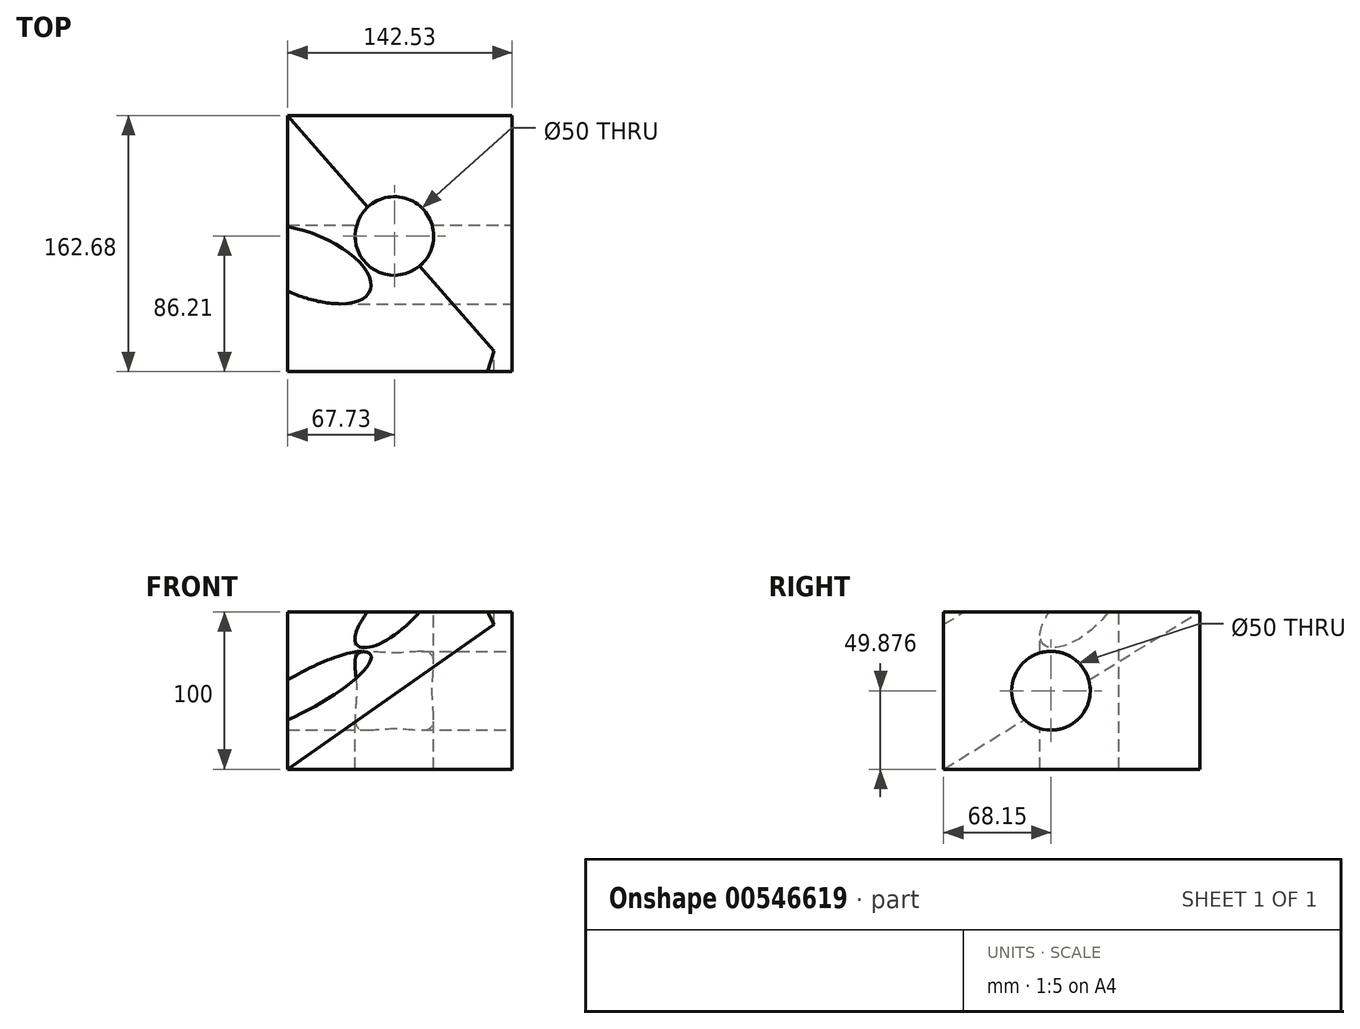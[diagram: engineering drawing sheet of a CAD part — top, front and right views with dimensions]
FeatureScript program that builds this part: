
annotation { "Feature Type Name" : "Feature", "Feature Type Description" : "" }
export const myFeature = defineFeature(function(context is Context, id is Id, definition is map)
    precondition{}
    {
        {
            var Q0;
            Q0=qCreatedBy(makeId("Top.planeOp"),FACE);
            var sketch = newSketch(context, id + "F0", { "sketchPlane" : qUnion([Q0])});
            skLineSegment(sketch, "E0.bottom", {"start": v(-67.73, -68.15) * mm, "end": v(74.8, -68.15) * mm});
            skLineSegment(sketch, "E0.top", {"start": v(-67.73, 94.53) * mm, "end": v(74.8, 94.53) * mm});
            skLineSegment(sketch, "E0.left", {"start": v(-67.73, -68.15) * mm, "end": v(-67.73, 94.53) * mm});
            skLineSegment(sketch, "E0.right", {"start": v(74.8, -68.15) * mm, "end": v(74.8, 94.53) * mm});
            skSolve(sketch);
        }
        {
            var Q0;
            Q0=makeQuery(id+"F0.imprint","IMPRINT",FACE,{"disambiguationData":[TD([[makeQuery(id+"F0.imprint","IMPRINT",EDGE,{"derivedFrom":sQuery(id+"F0.wireOp",EDGE,"E0.bottom")}),1.0]])]});
            extrude(context, id + "F1", {"entities" : qUnion([Q0]), "depth" : 100 * mm, "offsetDistance" : 25 * mm});
        }
        {
            var Q0;
            Q0=makeQuery(id+"F1.opExtrude","CAP_FACE",FACE,{"disambiguationData":[OSD([sQuery(id+"F0.wireOp",EDGE,"E0.bottom"),sQuery(id+"F0.wireOp",EDGE,"E0.top"),sQuery(id+"F0.wireOp",EDGE,"E0.left"),sQuery(id+"F0.wireOp",EDGE,"E0.right")])],"isStart":false});
            var sketch = newSketch(context, id + "F2", { "sketchPlane" : qUnion([Q0])});
            skPoint(sketch, "E1", {"position": v(0, 18.06) * mm});
            skSolve(sketch);
        }
        {
            var Q0;
            Q0=sQuery(id+"F2.wireOp",VERTEX,"E1");
            var Q1;
            Q1=makeQuery(id+"F1.opExtrude","SWEPT_BODY",BODY,{"disambiguationData":[OSD([sQuery(id+"F0.wireOp",EDGE,"E0.bottom"),sQuery(id+"F0.wireOp",EDGE,"E0.top"),sQuery(id+"F0.wireOp",EDGE,"E0.left"),sQuery(id+"F0.wireOp",EDGE,"E0.right")])]});
            hole(context, id + "F3", {"style" : HoleStyle.SIMPLE, "endStyle" : HoleEndStyle.THROUGH, "holeDiameter" : 50 * mm, "isTappedThrough" : true, "tappedDepth" : 12 * mm, "tapClearance" : 3, "locations" : qUnion([Q0]), "scope" : qUnion([Q1])});
        }
        {
            var Q0;
            Q0=makeQuery(id+"F1.opExtrude","SWEPT_FACE",FACE,{"disambiguationData":[OSD([sQuery(id+"F0.wireOp",EDGE,"E0.right")])]});
            var sketch = newSketch(context, id + "F4", { "sketchPlane" : qUnion([Q0])});
            skPoint(sketch, "E2", {"position": v(0, 49.88) * mm});
            skSolve(sketch);
        }
        {
            var Q0;
            Q0=sQuery(id+"F4.wireOp",VERTEX,"E2");
            var Q1;
            Q1=makeQuery(id+"F1.opExtrude","SWEPT_BODY",BODY,{"disambiguationData":[OSD([sQuery(id+"F0.wireOp",EDGE,"E0.bottom"),sQuery(id+"F0.wireOp",EDGE,"E0.top"),sQuery(id+"F0.wireOp",EDGE,"E0.left"),sQuery(id+"F0.wireOp",EDGE,"E0.right")])]});
            hole(context, id + "F5", {"style" : HoleStyle.SIMPLE, "endStyle" : HoleEndStyle.THROUGH, "holeDiameter" : 50 * mm, "isTappedThrough" : true, "tappedDepth" : 12 * mm, "tapClearance" : 3, "locations" : qUnion([Q0]), "scope" : qUnion([Q1])});
        }
        {
            var Q0;
            Q0=makeQuery(id+"F1.opExtrude","CAP_VERTEX",VERTEX,{"disambiguationData":[OSD([sQuery(id+"F0.wireOp",EDGE,"E0.top"),sQuery(id+"F0.wireOp",EDGE,"E0.left")])],"isStart":false});
            var Q1;
            Q1=makeQuery(id+"F1.opExtrude","CAP_VERTEX",VERTEX,{"disambiguationData":[OSD([sQuery(id+"F0.wireOp",EDGE,"E0.bottom"),sQuery(id+"F0.wireOp",EDGE,"E0.right")])],"isStart":false});
            var Q2;
            Q2=makeQuery(id+"F1.opExtrude","CAP_VERTEX",VERTEX,{"disambiguationData":[OSD([sQuery(id+"F0.wireOp",EDGE,"E0.bottom"),sQuery(id+"F0.wireOp",EDGE,"E0.left")])],"isStart":true});
            cPlane(context, id + "F6", {"entities" : qUnion([Q0, Q1, Q2]), "cplaneType" : CPlaneType.THREE_POINT, "offset" : 0 * mm, "width" : 150 * mm, "height" : 150 * mm});
        }
        {
            var Q0;
            Q0=qCreatedBy(id+"F6.planeOp",FACE);
            var sketch = newSketch(context, id + "F7", { "sketchPlane" : qUnion([Q0])});
            skLineSegment(sketch, "E3.bottom", {"start": v(-104.4, -99.8) * mm, "end": v(112.85, -99.8) * mm});
            skLineSegment(sketch, "E3.top", {"start": v(-104.4, 160.48) * mm, "end": v(112.85, 160.48) * mm});
            skLineSegment(sketch, "E3.left", {"start": v(-104.4, -99.8) * mm, "end": v(-104.4, 160.48) * mm});
            skLineSegment(sketch, "E3.right", {"start": v(112.85, -99.8) * mm, "end": v(112.85, 160.48) * mm});
            skSolve(sketch);
        }
        {
            var Q0;
            Q0=makeQuery(id+"F7.imprint","IMPRINT",FACE,{"disambiguationData":[TD([[makeQuery(id+"F7.imprint","IMPRINT",EDGE,{"derivedFrom":sQuery(id+"F7.wireOp",EDGE,"E3.bottom")}),1.0]])]});
            extrude(context, id + "F8", {"entities" : qUnion([Q0]), "operationType" : NewBodyOperationType.REMOVE, "depth" : 100 * mm, "offsetDistance" : 25 * mm});
        }
    });
